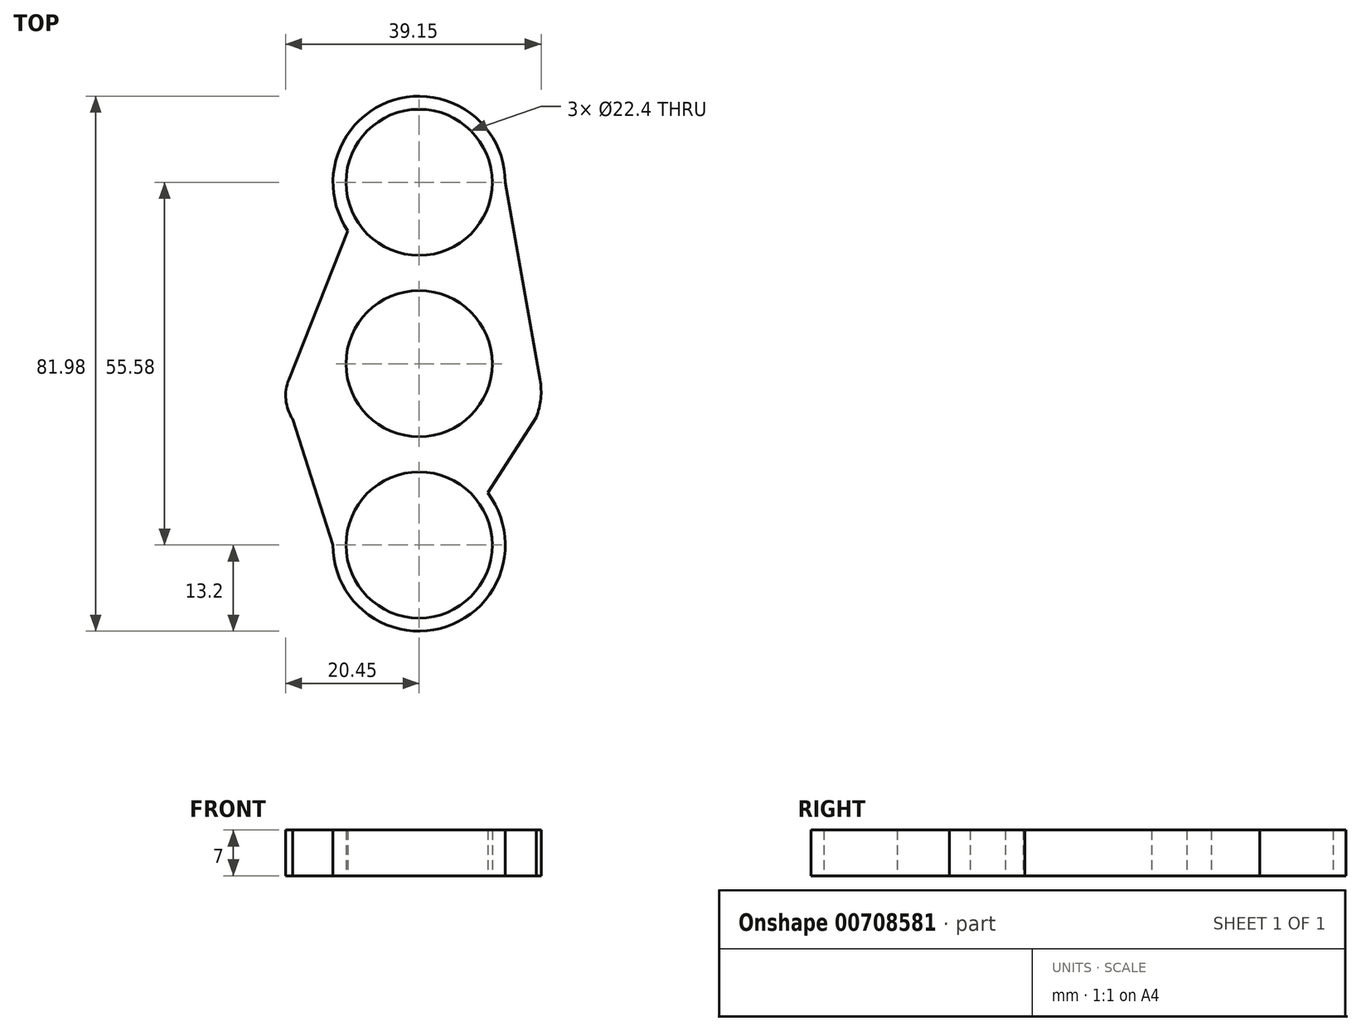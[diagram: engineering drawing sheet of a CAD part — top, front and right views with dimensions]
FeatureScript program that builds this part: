
annotation { "Feature Type Name" : "Feature", "Feature Type Description" : "" }
export const myFeature = defineFeature(function(context is Context, id is Id, definition is map)
    precondition{}
    {
        {
            var Q0;
            Q0=qCreatedBy(makeId("Top.planeOp"),FACE);
            var sketch = newSketch(context, id + "F0", { "sketchPlane" : qUnion([Q0])});
            skCircle(sketch, "E0", {"center": v(0, 0) * mm, "radius": 11.2 * mm});
            skCircle(sketch, "E1", {"center": v(0, 27.8) * mm, "radius": 11.2 * mm});
            skCircle(sketch, "E2.1.0", {"center": v(0, -27.8) * mm, "radius": 11.2 * mm});
            skArc(sketch, "E3", {"start": v(13.2, 27.8) * mm, "mid": v(-3.89, 40.4) * mm, "end": v(-10.91, 20.36) * mm});
            skArc(sketch, "E4", {"start": v(-13.2, -27.8) * mm, "mid": v(4.22, -40.3) * mm, "end": v(10.5, -19.8) * mm});
            skLineSegment(sketch, "E5", {"start": v(-10.91, 20.36) * mm, "end": v(-19.97, -2.44) * mm});
            skLineSegment(sketch, "E6", {"start": v(-13.2, -27.8) * mm, "end": v(-19.4, -8.48) * mm});
            skArc(sketch, "E7", {"start": v(-19.97, -2.44) * mm, "mid": v(-20.42, -5.53) * mm, "end": v(-19.4, -8.48) * mm});
            skLineSegment(sketch, "E8", {"start": v(13.2, 27.8) * mm, "end": v(18.54, -2.44) * mm});
            skLineSegment(sketch, "E9", {"start": v(10.5, -19.8) * mm, "end": v(17.96, -8.2) * mm});
            skArc(sketch, "E10", {"start": v(17.96, -8.2) * mm, "mid": v(18.65, -5.36) * mm, "end": v(18.54, -2.44) * mm});
            skSolve(sketch);
        }
        {
            var Q0;
            Q0 = qSketchRegion(id + "F0", true);
            extrude(context, id + "F1", {"entities" : qUnion([Q0]), "depth" : 7 * mm, "offsetDistance" : 25 * mm});
        }
    });
